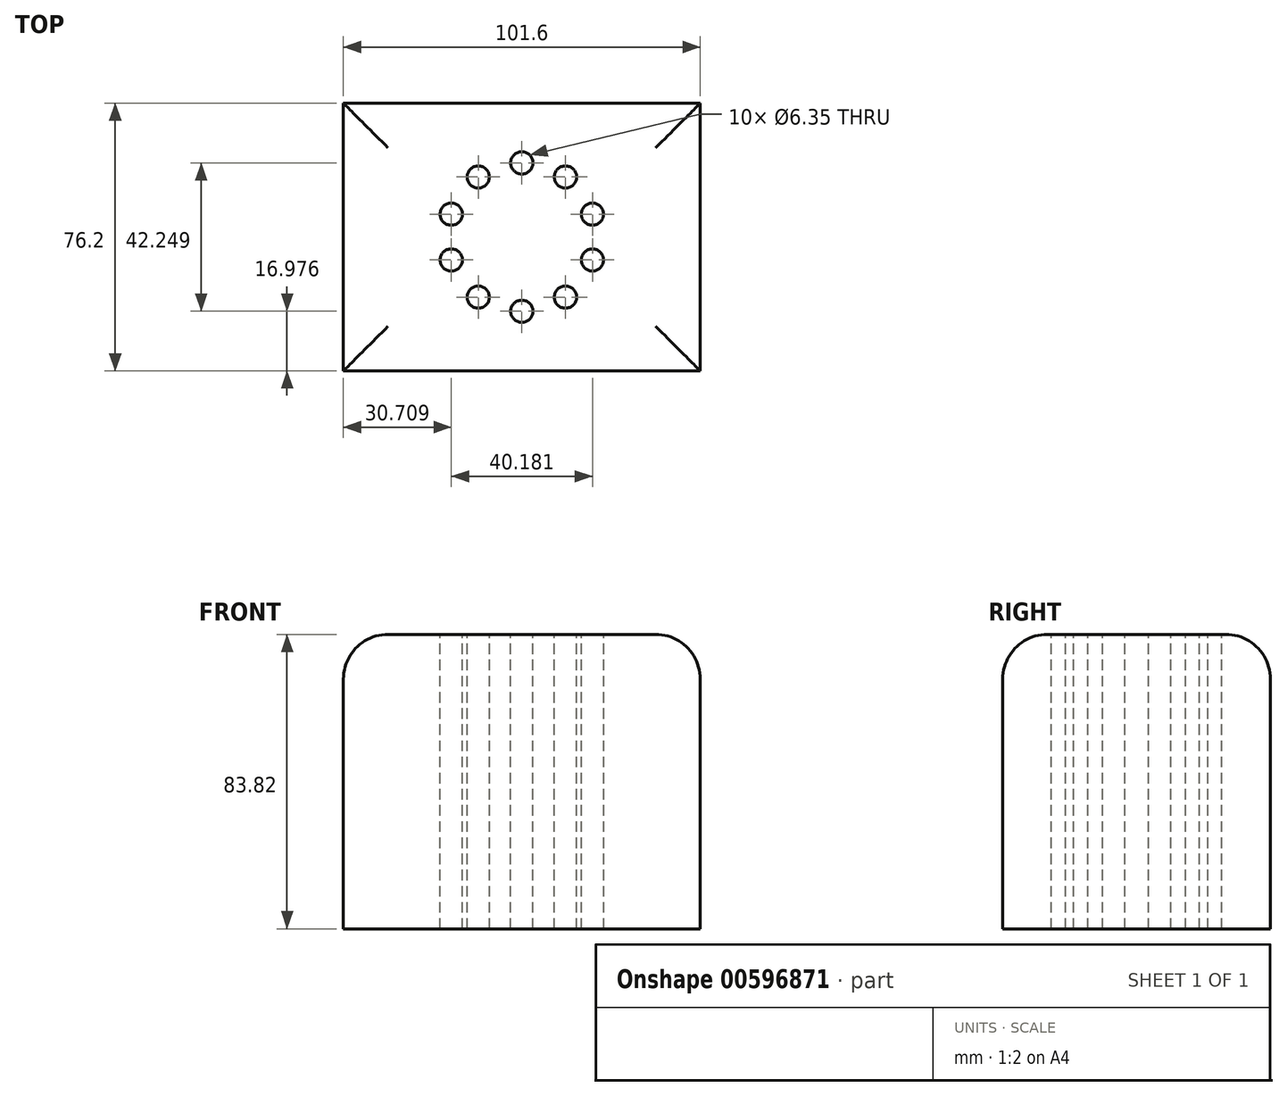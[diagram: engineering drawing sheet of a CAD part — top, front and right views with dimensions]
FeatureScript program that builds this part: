
annotation { "Feature Type Name" : "Feature", "Feature Type Description" : "" }
export const myFeature = defineFeature(function(context is Context, id is Id, definition is map)
    precondition{}
    {
        {
            var Q0;
            Q0=qCreatedBy(makeId("Top.planeOp"),FACE);
            var sketch = newSketch(context, id + "F0", { "sketchPlane" : qUnion([Q0])});
            skLineSegment(sketch, "E0.bottom", {"start": v(50.8, -38.1) * mm, "end": v(-50.8, -38.1) * mm});
            skLineSegment(sketch, "E0.top", {"start": v(50.8, 38.1) * mm, "end": v(-50.8, 38.1) * mm});
            skLineSegment(sketch, "E0.left", {"start": v(50.8, -38.1) * mm, "end": v(50.8, 38.1) * mm});
            skLineSegment(sketch, "E0.right", {"start": v(-50.8, -38.1) * mm, "end": v(-50.8, 38.1) * mm});
            skPoint(sketch, "E0.middle", {"position": v(0, 0) * mm});
            skSolve(sketch);
        }
        {
            var Q0;
            Q0=makeQuery(id+"F0.imprint","IMPRINT",FACE,{"disambiguationData":[TD([[makeQuery(id+"F0.imprint","IMPRINT",EDGE,{"derivedFrom":sQuery(id+"F0.wireOp",EDGE,"E0.bottom")}),-1.0]])]});
            extrude(context, id + "F1", {"entities" : qUnion([Q0]), "depth" : 83.82 * mm, "offsetDistance" : 25.4 * mm});
        }
        {
            var Q0;
            Q0=makeQuery(id+"F1.opExtrude","CAP_EDGE",EDGE,{"disambiguationData":[OSD([sQuery(id+"F0.wireOp",EDGE,"E0.bottom")])],"isStart":false});
            var Q1;
            Q1=makeQuery(id+"F1.opExtrude","CAP_EDGE",EDGE,{"disambiguationData":[OSD([sQuery(id+"F0.wireOp",EDGE,"E0.left")])],"isStart":false});
            var Q2;
            Q2=makeQuery(id+"F1.opExtrude","CAP_EDGE",EDGE,{"disambiguationData":[OSD([sQuery(id+"F0.wireOp",EDGE,"E0.top")])],"isStart":false});
            var Q3;
            Q3=makeQuery(id+"F1.opExtrude","CAP_EDGE",EDGE,{"disambiguationData":[OSD([sQuery(id+"F0.wireOp",EDGE,"E0.right")])],"isStart":false});
            fillet(context, id + "F2", {"entities" : qUnion([Q0, Q1, Q2, Q3]), "radius" : 12.7 * mm, "tangentPropagation" : true, "allowEdgeOverflow" : false});
        }
        {
            var Q0;
            Q0=makeQuery(id+"F1.opExtrude","CAP_FACE",FACE,{"disambiguationData":[OSD([sQuery(id+"F0.wireOp",EDGE,"E0.bottom"),sQuery(id+"F0.wireOp",EDGE,"E0.top"),sQuery(id+"F0.wireOp",EDGE,"E0.left"),sQuery(id+"F0.wireOp",EDGE,"E0.right")])],"isStart":false});
            var sketch = newSketch(context, id + "F3", { "sketchPlane" : qUnion([Q0])});
            skCircle(sketch, "E1", {"center": v(0, 0) * mm, "radius": 19.05 * mm});
            skSolve(sketch);
        }
        {
            var Q0;
            Q0=makeQuery(id+"F3.imprint","IMPRINT",FACE,{"disambiguationData":[TD([[makeQuery(id+"F3.imprint","IMPRINT",EDGE,{"derivedFrom":sQuery(id+"F3.wireOp",EDGE,"E1")}),1.0]])]});
            var sketch = newSketch(context, id + "F4", { "sketchPlane" : qUnion([Q0])});
            skCircle(sketch, "E2.cCircle", {"center": v(0, 0) * mm, "radius": 20.1 * mm, "construction": true});
            skLineSegment(sketch, "E2.0", {"start": v(20.1, 6.53) * mm, "end": v(20.1, -6.53) * mm});
            skLineSegment(sketch, "E2.1", {"start": v(20.1, -6.53) * mm, "end": v(12.42, -17.1) * mm});
            skLineSegment(sketch, "E2.2", {"start": v(12.42, -17.1) * mm, "end": v(0, -21.12) * mm});
            skLineSegment(sketch, "E2.3", {"start": v(0, -21.12) * mm, "end": v(-12.42, -17.1) * mm});
            skLineSegment(sketch, "E2.4", {"start": v(-12.42, -17.1) * mm, "end": v(-20.1, -6.53) * mm});
            skLineSegment(sketch, "E2.5", {"start": v(-20.1, -6.53) * mm, "end": v(-20.1, 6.53) * mm});
            skLineSegment(sketch, "E2.6", {"start": v(-20.1, 6.53) * mm, "end": v(-12.42, 17.1) * mm});
            skLineSegment(sketch, "E2.7", {"start": v(-12.42, 17.1) * mm, "end": v(0, 21.12) * mm});
            skLineSegment(sketch, "E2.8", {"start": v(0, 21.12) * mm, "end": v(12.42, 17.1) * mm});
            skLineSegment(sketch, "E2.9", {"start": v(12.42, 17.1) * mm, "end": v(20.1, 6.53) * mm});
            skPoint(sketch, "E2.0.midPoint", {"position": v(20.1, 0) * mm});
            skSolve(sketch);
        }
        {
            var Q0;
            Q0=sQuery(id+"F4.wireOp",VERTEX,"E2.2.start");
            var Q1;
            Q1=sQuery(id+"F4.wireOp",VERTEX,"E2.3.start");
            var Q2;
            Q2=sQuery(id+"F4.wireOp",VERTEX,"E2.4.start");
            var Q3;
            Q3=sQuery(id+"F4.wireOp",VERTEX,"E2.5.start");
            var Q4;
            Q4=sQuery(id+"F4.wireOp",VERTEX,"E2.6.start");
            var Q5;
            Q5=sQuery(id+"F4.wireOp",VERTEX,"E2.7.start");
            var Q6;
            Q6=sQuery(id+"F4.wireOp",VERTEX,"E2.8.start");
            var Q7;
            Q7=sQuery(id+"F4.wireOp",VERTEX,"E2.8.end");
            var Q8;
            Q8=sQuery(id+"F4.wireOp",VERTEX,"E2.0.start");
            var Q9;
            Q9=sQuery(id+"F4.wireOp",VERTEX,"E2.1.start");
            var Q10;
            Q10=makeQuery(id+"F1.opExtrude","SWEPT_BODY",BODY,{"disambiguationData":[OSD([sQuery(id+"F0.wireOp",EDGE,"E0.bottom"),sQuery(id+"F0.wireOp",EDGE,"E0.top"),sQuery(id+"F0.wireOp",EDGE,"E0.left"),sQuery(id+"F0.wireOp",EDGE,"E0.right")])]});
            hole(context, id + "F5", {"style" : HoleStyle.SIMPLE, "endStyle" : HoleEndStyle.THROUGH, "holeDiameter" : 6.35 * mm, "majorDiameter" : 6.35 * mm, "isTappedThrough" : true, "tappedDepth" : 12.7 * mm, "tapClearance" : 3, "locations" : qUnion([Q0, Q1, Q2, Q3, Q4, Q5, Q6, Q7, Q8, Q9]), "scope" : qUnion([Q10])});
        }
    });
